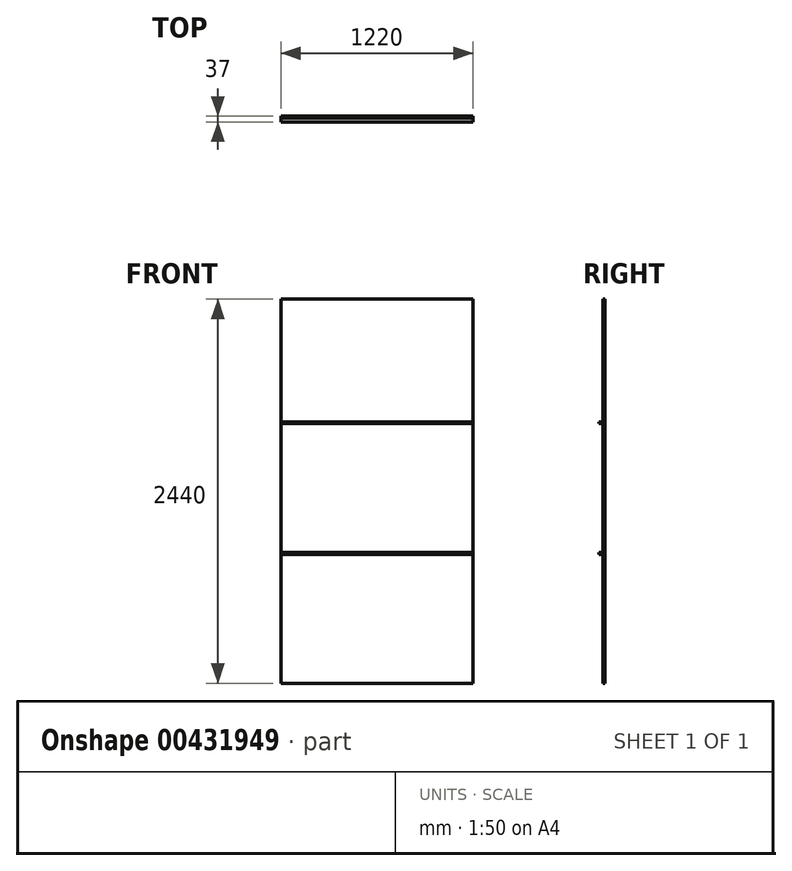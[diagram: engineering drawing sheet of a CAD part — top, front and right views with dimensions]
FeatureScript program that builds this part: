
annotation { "Feature Type Name" : "Feature", "Feature Type Description" : "" }
export const myFeature = defineFeature(function(context is Context, id is Id, definition is map)
    precondition{}
    {
        {
            var Q0;
            Q0=qCreatedBy(makeId("Front.planeOp"),FACE);
            var sketch = newSketch(context, id + "F0", { "sketchPlane" : qUnion([Q0])});
            skLineSegment(sketch, "E0.bottom", {"start": v(0, 0) * mm, "end": v(-1220, 0) * mm});
            skLineSegment(sketch, "E0.top", {"start": v(0, 2440) * mm, "end": v(-1220, 2440) * mm});
            skLineSegment(sketch, "E0.left", {"start": v(0, 0) * mm, "end": v(0, 2440) * mm});
            skLineSegment(sketch, "E0.right", {"start": v(-1220, 0) * mm, "end": v(-1220, 2440) * mm});
            skSolve(sketch);
        }
        {
            var Q0;
            Q0=makeQuery(id+"F0.imprint","IMPRINT",FACE,{"disambiguationData":[TD([[makeQuery(id+"F0.imprint","IMPRINT",EDGE,{"derivedFrom":sQuery(id+"F0.wireOp",EDGE,"E0.bottom")}),-1.0]])]});
            extrude(context, id + "F1", {"entities" : qUnion([Q0]), "depth" : 12 * mm, "offsetDistance" : 25 * mm});
        }
        {
            var Q0;
            Q0=makeQuery(id+"F1.opExtrude","CAP_FACE",FACE,{"disambiguationData":[OSD([sQuery(id+"F0.wireOp",EDGE,"E0.bottom"),sQuery(id+"F0.wireOp",EDGE,"E0.top"),sQuery(id+"F0.wireOp",EDGE,"E0.left"),sQuery(id+"F0.wireOp",EDGE,"E0.right")])],"isStart":false});
            var sketch = newSketch(context, id + "F2", { "sketchPlane" : qUnion([Q0])});
            skLineSegment(sketch, "E1.bottom", {"start": v(-1220, 830) * mm, "end": v(0, 830) * mm});
            skLineSegment(sketch, "E1.top", {"start": v(-1220, 820) * mm, "end": v(0, 820) * mm});
            skLineSegment(sketch, "E1.left", {"start": v(-1220, 830) * mm, "end": v(-1220, 820) * mm});
            skLineSegment(sketch, "E1.right", {"start": v(0, 830) * mm, "end": v(0, 820) * mm});
            skLineSegment(sketch, "E2.bottom", {"start": v(-1220, 1660) * mm, "end": v(0, 1660) * mm});
            skLineSegment(sketch, "E2.top", {"start": v(-1220, 1650) * mm, "end": v(0, 1650) * mm});
            skLineSegment(sketch, "E2.left", {"start": v(-1220, 1660) * mm, "end": v(-1220, 1650) * mm});
            skLineSegment(sketch, "E2.right", {"start": v(0, 1660) * mm, "end": v(0, 1650) * mm});
            skSolve(sketch);
        }
        {
            var Q0;
            Q0 = qSketchRegion(id + "F2", true);
            extrude(context, id + "F3", {"entities" : qUnion([Q0]), "operationType" : NewBodyOperationType.ADD, "depth" : 25 * mm, "offsetDistance" : 25 * mm});
        }
    });
